# Revit family: Mixer tap-Wall_mounted-PRESTO-MURAL NEO FROID 95MM 15SEC-66010
name_source: partatom
category: Plumbing Fixtures
revit_build: Autodesk Revit Architecture 2014 (Build: 20130308_1515(x64)
units: mm (PartAtom-declared; Revit-internal decimal feet)

## types (1)
- 66010
    Description = PRESTO NEO Robinet simple temporisé mural (95mm)
    Durée = 15.0 s
    Durée (réglage à 4 positions) = 15 secondes (± 5 sec.)
    Débit (à 3 bar - régulateur de débit à 4 positions) = 3 l/min à 3 bar
    Edition number = 1
    Entrée EC = 0 mm  [stored 0 ft]
    Entrée EF = 13 mm
    Garantie = 10
    HW Connection = Yes
    Hauteur = 0 mm  [stored 0 ft]
    Largeur = 134 mm
    Lenght = 0 mm  [stored 0 ft]
    Manufacturer = PRESTO LES ROBINETS
    Manufacturer name = Presto
    Material main = Brass
    Material secondary = Chrome
    Matériau Principal = Corps en laiton, conforme aux normes NE 1982, NE 12164, NE 12156
    Matériau Secondare = Corps moulé chromé conforme à la norme NE 12540
    Model = 66010
    Nominal height = 13400
    Nominal width = 0
    Pression de fonctionnement = 1 à 5 bar
    Product Guid = ea6e7263-f6e2-4606-ba86-a94ccf08a650
    Product SKU = 66010
    Product data url = http://bimobject.com
    Product family = NEO
    Product group = ROBINET
    QR code = http://bimobject.com
    Temp - Résistance (Choc Thermique de 30 Minutes) = 75 °C
    Weight Net (Kg) = 0

note: [stored X ft] marks values corroborated as IEEE doubles in the binary element streams (Revit-internal decimal feet)

## geometry (parser evidence)
native form markers: Blend x2, Sweep x20
no freeform markers — native parametric forms only
